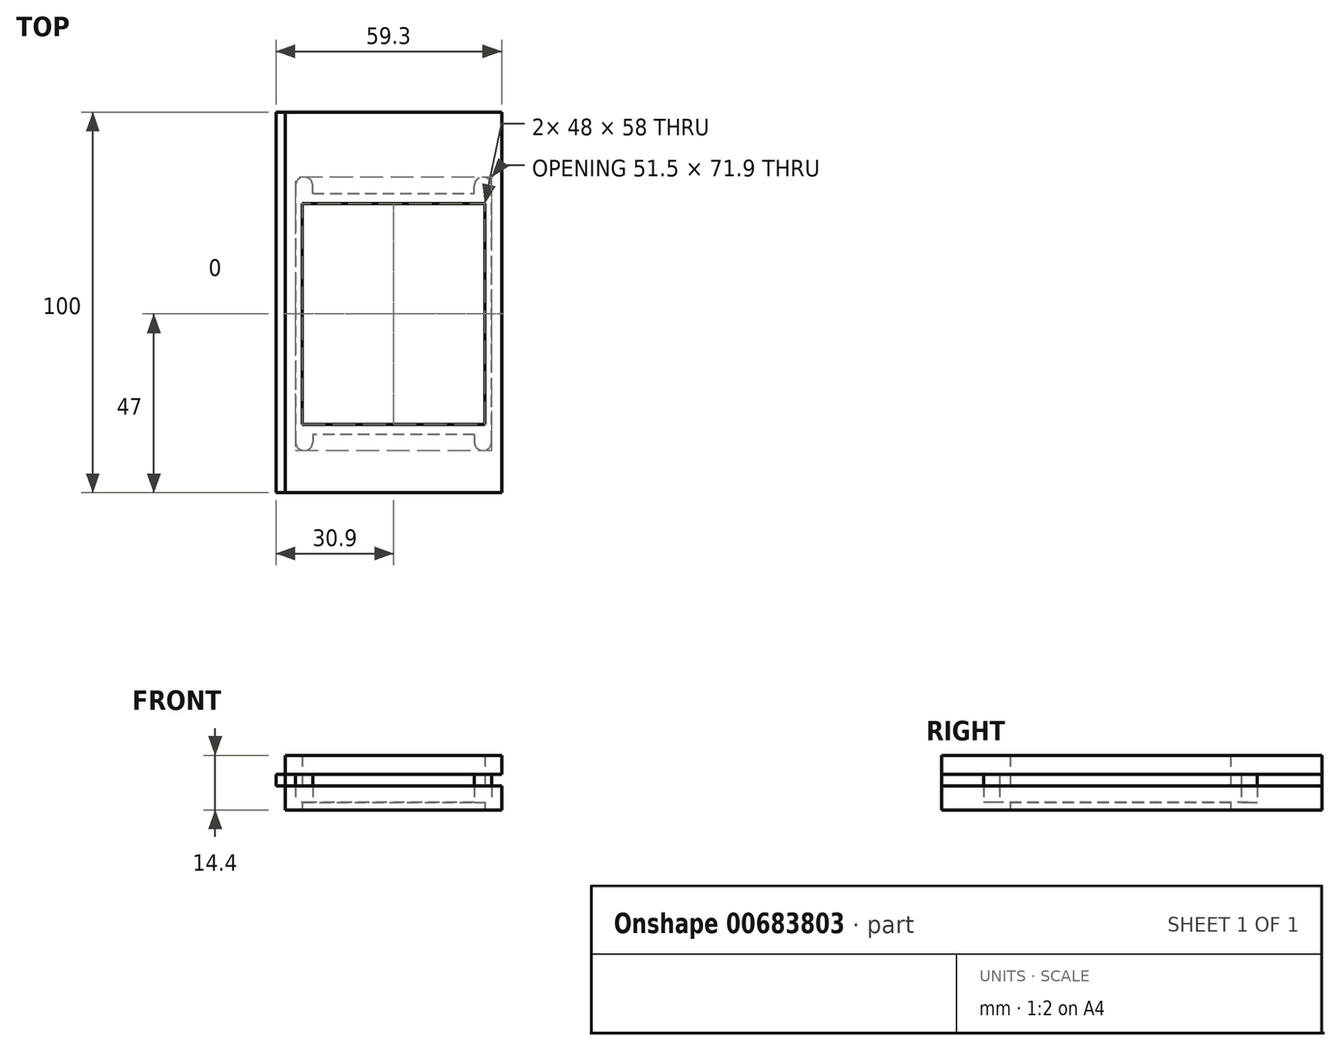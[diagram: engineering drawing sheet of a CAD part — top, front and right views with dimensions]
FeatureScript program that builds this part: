
annotation { "Feature Type Name" : "Feature", "Feature Type Description" : "" }
export const myFeature = defineFeature(function(context is Context, id is Id, definition is map)
    precondition{}
    {
        {
            var Q0;
            Q0=qCreatedBy(makeId("Top.planeOp"),FACE);
            var sketch = newSketch(context, id + "F0", { "sketchPlane" : qUnion([Q0])});
            skLineSegment(sketch, "E0", {"start": v(0, 0) * mm, "end": v(-28.4, 0) * mm});
            skLineSegment(sketch, "E1", {"start": v(-28.4, 0) * mm, "end": v(-28.4, 100) * mm});
            skLineSegment(sketch, "E2", {"start": v(-28.4, 100) * mm, "end": v(0, 100) * mm});
            skLineSegment(sketch, "E3.MirrorCS", {"start": v(0, 0) * mm, "end": v(28.4, 0) * mm});
            skLineSegment(sketch, "E4.MirrorCS", {"start": v(28.4, 100) * mm, "end": v(0, 100) * mm});
            skLineSegment(sketch, "E5.MirrorCS", {"start": v(28.4, 0) * mm, "end": v(28.4, 100) * mm});
            skLineSegment(sketch, "E6", {"start": v(0, 18) * mm, "end": v(-24, 18) * mm});
            skLineSegment(sketch, "E7", {"start": v(-24, 18) * mm, "end": v(-24, 76) * mm});
            skLineSegment(sketch, "E8", {"start": v(-24, 76) * mm, "end": v(0, 76) * mm});
            skLineSegment(sketch, "E9.MirrorCS", {"start": v(0, 18) * mm, "end": v(24, 18) * mm});
            skLineSegment(sketch, "E10.MirrorCS", {"start": v(24, 76) * mm, "end": v(0, 76) * mm});
            skLineSegment(sketch, "E11.MirrorCS", {"start": v(24, 18) * mm, "end": v(24, 76) * mm});
            skSolve(sketch);
        }
        {
            var Q0;
            Q0=makeQuery(id+"F0.imprint","IMPRINT",FACE,{"disambiguationData":[TD([[makeQuery(id+"F0.imprint","IMPRINT",EDGE,{"derivedFrom":sQuery(id+"F0.wireOp",EDGE,"E0")}),-1.0]])]});
            extrude(context, id + "F1", {"entities" : qUnion([Q0]), "depth" : 2 * mm, "offsetDistance" : 25 * mm});
        }
        {
            var Q0;
            Q0=makeQuery(id+"F1.opExtrude","CAP_FACE",FACE,{"disambiguationData":[OSD([sQuery(id+"F0.wireOp",EDGE,"E0"),sQuery(id+"F0.wireOp",EDGE,"E1"),sQuery(id+"F0.wireOp",EDGE,"E2"),sQuery(id+"F0.wireOp",EDGE,"E3.MirrorCS"),sQuery(id+"F0.wireOp",EDGE,"E4.MirrorCS"),sQuery(id+"F0.wireOp",EDGE,"E5.MirrorCS"),sQuery(id+"F0.wireOp",EDGE,"E6"),sQuery(id+"F0.wireOp",EDGE,"E7"),sQuery(id+"F0.wireOp",EDGE,"E8"),sQuery(id+"F0.wireOp",EDGE,"E9.MirrorCS"),sQuery(id+"F0.wireOp",EDGE,"E10.MirrorCS"),sQuery(id+"F0.wireOp",EDGE,"E11.MirrorCS")])],"isStart":false});
            var sketch = newSketch(context, id + "F2", { "sketchPlane" : qUnion([Q0])});
            skLineSegment(sketch, "E12.0", {"start": v(28.4, 100) * mm, "end": v(-28.4, 100) * mm});
            skLineSegment(sketch, "E12.1", {"start": v(-28.4, 0) * mm, "end": v(-28.4, 100) * mm});
            skLineSegment(sketch, "E12.2", {"start": v(28.4, 0) * mm, "end": v(28.4, 100) * mm});
            skLineSegment(sketch, "E12.3", {"start": v(-28.4, 0) * mm, "end": v(28.4, 0) * mm});
            skLineSegment(sketch, "E13", {"start": v(-25.75, 78.7) * mm, "end": v(-25.75, 15.3) * mm});
            skLineSegment(sketch, "E14", {"start": v(-21.25, 78.7) * mm, "end": v(0, 78.7) * mm});
            skLineSegment(sketch, "E15", {"start": v(-25.75, 78.7) * mm, "end": v(-25.75, 80.7) * mm});
            skArc(sketch, "E16", {"start": v(-21.25, 80.7) * mm, "mid": v(-23.5, 82.95) * mm, "end": v(-25.75, 80.7) * mm});
            skLineSegment(sketch, "E17", {"start": v(-21.25, 78.7) * mm, "end": v(-21.25, 80.7) * mm});
            skLineSegment(sketch, "E18", {"start": v(-25.75, 15.3) * mm, "end": v(-25.75, 13.3) * mm});
            skLineSegment(sketch, "E19", {"start": v(-21.25, 15.3) * mm, "end": v(-21.25, 13.3) * mm});
            skArc(sketch, "E20", {"start": v(-25.75, 13.3) * mm, "mid": v(-23.5, 11.05) * mm, "end": v(-21.25, 13.3) * mm});
            skLineSegment(sketch, "E21.trimOffspring", {"start": v(-21.25, 15.3) * mm, "end": v(0, 15.3) * mm});
            skLineSegment(sketch, "E22.MirrorCS", {"start": v(21.25, 15.3) * mm, "end": v(0, 15.3) * mm});
            skLineSegment(sketch, "E23.MirrorCS", {"start": v(21.25, 15.3) * mm, "end": v(21.25, 13.3) * mm});
            skArc(sketch, "E24.MirrorCS", {"start": v(25.75, 13.3) * mm, "mid": v(23.5, 11.05) * mm, "end": v(21.25, 13.3) * mm});
            skLineSegment(sketch, "E25.MirrorCS", {"start": v(25.75, 15.3) * mm, "end": v(25.75, 13.3) * mm});
            skLineSegment(sketch, "E26.MirrorCS", {"start": v(25.75, 78.7) * mm, "end": v(25.75, 15.3) * mm});
            skLineSegment(sketch, "E27.MirrorCS", {"start": v(25.75, 78.7) * mm, "end": v(25.75, 80.7) * mm});
            skArc(sketch, "E28.MirrorCS", {"start": v(21.25, 80.7) * mm, "mid": v(23.5, 82.95) * mm, "end": v(25.75, 80.7) * mm});
            skLineSegment(sketch, "E29.MirrorCS", {"start": v(21.25, 78.7) * mm, "end": v(0, 78.7) * mm});
            skLineSegment(sketch, "E30.MirrorCS", {"start": v(21.25, 78.7) * mm, "end": v(21.25, 80.7) * mm});
            skSolve(sketch);
        }
        {
            var Q0;
            Q0=makeQuery(id+"F2.imprint","IMPRINT",FACE,{"disambiguationData":[TD([[makeQuery(id+"F2.imprint","IMPRINT",EDGE,{"derivedFrom":sQuery(id+"F2.wireOp",EDGE,"E12.0")}),1.0]])]});
            extrude(context, id + "F3", {"entities" : qUnion([Q0]), "operationType" : NewBodyOperationType.ADD, "depth" : 4.4 * mm, "offsetDistance" : 25 * mm});
        }
        {
            var Q0;
            Q0=makeQuery(id+"F3.opExtrude","CAP_FACE",FACE,{"disambiguationData":[OSD([sQuery(id+"F2.wireOp",EDGE,"E12.0"),sQuery(id+"F2.wireOp",EDGE,"E12.1"),sQuery(id+"F2.wireOp",EDGE,"E12.2"),sQuery(id+"F2.wireOp",EDGE,"E12.3"),sQuery(id+"F2.wireOp",EDGE,"E13"),sQuery(id+"F2.wireOp",EDGE,"E14"),sQuery(id+"F2.wireOp",EDGE,"E15"),sQuery(id+"F2.wireOp",EDGE,"E16"),sQuery(id+"F2.wireOp",EDGE,"E17"),sQuery(id+"F2.wireOp",EDGE,"E18"),sQuery(id+"F2.wireOp",EDGE,"E19"),sQuery(id+"F2.wireOp",EDGE,"E20"),sQuery(id+"F2.wireOp",EDGE,"E21.trimOffspring"),sQuery(id+"F2.wireOp",EDGE,"E22.MirrorCS"),sQuery(id+"F2.wireOp",EDGE,"E23.MirrorCS"),sQuery(id+"F2.wireOp",EDGE,"E24.MirrorCS"),sQuery(id+"F2.wireOp",EDGE,"E25.MirrorCS"),sQuery(id+"F2.wireOp",EDGE,"E26.MirrorCS"),sQuery(id+"F2.wireOp",EDGE,"E27.MirrorCS"),sQuery(id+"F2.wireOp",EDGE,"E28.MirrorCS"),sQuery(id+"F2.wireOp",EDGE,"E29.MirrorCS"),sQuery(id+"F2.wireOp",EDGE,"E30.MirrorCS")])],"isStart":false});
            var sketch = newSketch(context, id + "F4", { "sketchPlane" : qUnion([Q0])});
            skLineSegment(sketch, "E31.0", {"start": v(21.25, 78.7) * mm, "end": v(-21.25, 78.7) * mm});
            skLineSegment(sketch, "E31.1", {"start": v(25.75, 15.3) * mm, "end": v(25.75, 78.7) * mm});
            skLineSegment(sketch, "E31.2", {"start": v(-25.75, 78.7) * mm, "end": v(-25.75, 15.3) * mm});
            skLineSegment(sketch, "E31.3", {"start": v(21.25, 15.3) * mm, "end": v(-21.25, 15.3) * mm});
            skLineSegment(sketch, "E32", {"start": v(-21.25, 15.3) * mm, "end": v(-25.75, 15.3) * mm});
            skPoint(sketch, "E33.orphan", {"position": v(-25.75, 13.3) * mm});
            skLineSegment(sketch, "E34", {"start": v(-21.25, 78.7) * mm, "end": v(-25.75, 78.7) * mm});
            skLineSegment(sketch, "E35", {"start": v(21.25, 78.7) * mm, "end": v(25.75, 78.7) * mm});
            skLineSegment(sketch, "E36", {"start": v(21.25, 15.3) * mm, "end": v(25.75, 15.3) * mm});
            skPoint(sketch, "E37.orphan", {"position": v(-25.75, 80.7) * mm});
            skPoint(sketch, "E38.orphan", {"position": v(25.75, 80.7) * mm});
            skPoint(sketch, "E39.orphan", {"position": v(25.75, 13.3) * mm});
            skLineSegment(sketch, "E40.0", {"start": v(-24, 76) * mm, "end": v(24, 76) * mm});
            skLineSegment(sketch, "E40.1", {"start": v(-24, 18) * mm, "end": v(-24, 76) * mm});
            skLineSegment(sketch, "E40.2", {"start": v(-24, 18) * mm, "end": v(24, 18) * mm});
            skLineSegment(sketch, "E40.3", {"start": v(24, 18) * mm, "end": v(24, 76) * mm});
            skSolve(sketch);
        }
        {
            var Q0;
            Q0=makeQuery(id+"F4.imprint","IMPRINT",FACE,{"disambiguationData":[TD([[makeQuery(id+"F4.imprint","IMPRINT",EDGE,{"derivedFrom":sQuery(id+"F4.wireOp",EDGE,"E31.0")}),1.0]])]});
            extrude(context, id + "F5", {"entities" : qUnion([Q0]), "oppositeDirection" : true, "depth" : 3 * mm, "offsetDistance" : 25 * mm});
        }
        {
            var Q0;
            Q0=makeQuery(id+"F5.opExtrude","CAP_FACE",FACE,{"disambiguationData":[OSD([sQuery(id+"F4.wireOp",EDGE,"E31.0"),sQuery(id+"F4.wireOp",EDGE,"E31.1"),sQuery(id+"F4.wireOp",EDGE,"E31.2"),sQuery(id+"F4.wireOp",EDGE,"E31.3"),sQuery(id+"F4.wireOp",EDGE,"E32"),sQuery(id+"F4.wireOp",EDGE,"E34"),sQuery(id+"F4.wireOp",EDGE,"E35"),sQuery(id+"F4.wireOp",EDGE,"E36")])],"isStart":true});
            var sketch = newSketch(context, id + "F6", { "sketchPlane" : qUnion([Q0])});
            skLineSegment(sketch, "E41.0", {"start": v(28.4, 100) * mm, "end": v(-28.4, 100) * mm});
            skLineSegment(sketch, "E41.1", {"start": v(-28.4, 0) * mm, "end": v(28.4, 0) * mm});
            skLineSegment(sketch, "E42", {"start": v(0, 0) * mm, "end": v(-30.9, 0) * mm});
            skLineSegment(sketch, "E43", {"start": v(-30.9, 0) * mm, "end": v(-30.9, 100) * mm});
            skLineSegment(sketch, "E44", {"start": v(-30.9, 100) * mm, "end": v(0, 100) * mm});
            skLineSegment(sketch, "E45.MirrorCS", {"start": v(0, 0) * mm, "end": v(30.9, 0) * mm});
            skLineSegment(sketch, "E46.MirrorCS", {"start": v(30.9, 100) * mm, "end": v(0, 100) * mm});
            skLineSegment(sketch, "E47.MirrorCS", {"start": v(30.9, 0) * mm, "end": v(30.9, 100) * mm});
            skLineSegment(sketch, "E48.0", {"start": v(-24, 76) * mm, "end": v(24, 76) * mm});
            skLineSegment(sketch, "E48.1", {"start": v(24, 18) * mm, "end": v(24, 76) * mm});
            skLineSegment(sketch, "E48.2", {"start": v(-24, 18) * mm, "end": v(24, 18) * mm});
            skLineSegment(sketch, "E48.3", {"start": v(-24, 18) * mm, "end": v(-24, 76) * mm});
            skSolve(sketch);
        }
        {
            var Q0;
            {var subQ5=sQuery(id+"F6.wireOp",EDGE,"E43");Q0=makeQuery(id+"F6.imprint","IMPRINT",FACE,{"disambiguationData":[TD([[makeQuery(id+"F6.imprint","IMPRINT",EDGE,{"derivedFrom":subQ5}),-1.0]])]});}
            var Q1;
            Q1=makeQuery(id+"F6.imprint","IMPRINT",FACE,{"disambiguationData":[TD([[makeQuery(id+"F6.imprint","IMPRINT",EDGE,{"derivedFrom":sQuery(id+"F6.wireOp",EDGE,"E48.0")}),1.0]])]});
            extrude(context, id + "F7", {"entities" : qUnion([Q0, Q1]), "operationType" : NewBodyOperationType.ADD, "depth" : 3 * mm, "offsetDistance" : 25 * mm});
        }
        {
            var Q0;
            Q0=makeQuery(id+"F7.opExtrude","CAP_FACE",FACE,{"disambiguationData":[OSD([sQuery(id+"F6.wireOp",EDGE,"E42"),sQuery(id+"F6.wireOp",EDGE,"E43"),sQuery(id+"F6.wireOp",EDGE,"E44"),sQuery(id+"F6.wireOp",EDGE,"E45.MirrorCS"),sQuery(id+"F6.wireOp",EDGE,"E46.MirrorCS"),sQuery(id+"F6.wireOp",EDGE,"E47.MirrorCS")])],"isStart":false});
            var sketch = newSketch(context, id + "F8", { "sketchPlane" : qUnion([Q0])});
            skLineSegment(sketch, "E49.bottom", {"start": v(-28.4, 100) * mm, "end": v(28.4, 100) * mm});
            skLineSegment(sketch, "E49.top", {"start": v(-28.4, 0) * mm, "end": v(28.4, 0) * mm});
            skLineSegment(sketch, "E49.left", {"start": v(-28.4, 100) * mm, "end": v(-28.4, 0) * mm});
            skLineSegment(sketch, "E49.right", {"start": v(28.4, 100) * mm, "end": v(28.4, 0) * mm});
            skLineSegment(sketch, "E50.0", {"start": v(-24, 76) * mm, "end": v(24, 76) * mm});
            skLineSegment(sketch, "E50.1", {"start": v(24, 18) * mm, "end": v(24, 76) * mm});
            skLineSegment(sketch, "E50.2", {"start": v(-24, 18) * mm, "end": v(24, 18) * mm});
            skLineSegment(sketch, "E50.3", {"start": v(-24, 18) * mm, "end": v(-24, 76) * mm});
            skSolve(sketch);
        }
        {
            var Q0;
            Q0 = qSketchRegion(id + "F8", true);
            extrude(context, id + "F9", {"entities" : qUnion([Q0]), "operationType" : NewBodyOperationType.ADD, "depth" : 5 * mm, "offsetDistance" : 25 * mm});
        }
    });
